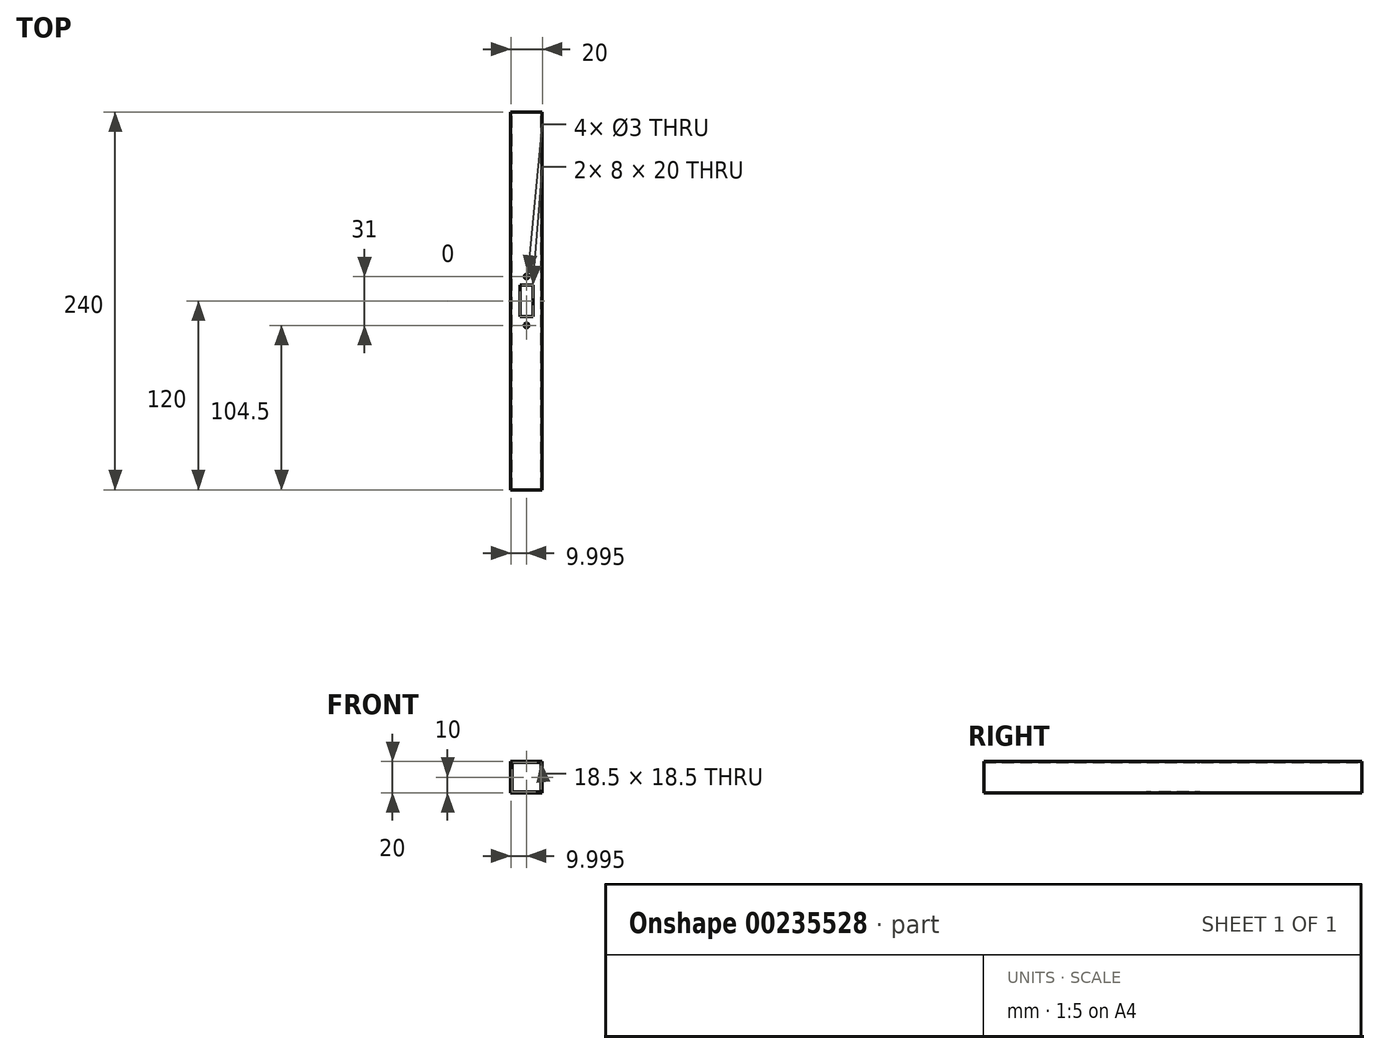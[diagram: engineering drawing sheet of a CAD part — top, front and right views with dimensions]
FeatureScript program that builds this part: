
annotation { "Feature Type Name" : "Feature", "Feature Type Description" : "" }
export const myFeature = defineFeature(function(context is Context, id is Id, definition is map)
    precondition{}
    {
        {
            var Q0;
            Q0=qCreatedBy(makeId("Front.planeOp"),FACE);
            var sketch = newSketch(context, id + "F0", { "sketchPlane" : qUnion([Q0])});
            skLineSegment(sketch, "E0.bottom", {"start": v(-34.48, 27) * mm, "end": v(-54.48, 27) * mm});
            skLineSegment(sketch, "E0.top", {"start": v(-34.48, 47) * mm, "end": v(-54.48, 47) * mm});
            skLineSegment(sketch, "E0.left", {"start": v(-34.48, 27) * mm, "end": v(-34.48, 47) * mm});
            skLineSegment(sketch, "E0.right", {"start": v(-54.48, 27) * mm, "end": v(-54.48, 47) * mm});
            skPoint(sketch, "E0.middle", {"position": v(-44.48, 37) * mm});
            skLineSegment(sketch, "E1.bottom", {"start": v(-35.23, 27.75) * mm, "end": v(-53.73, 27.75) * mm});
            skLineSegment(sketch, "E1.top", {"start": v(-35.23, 46.25) * mm, "end": v(-53.73, 46.25) * mm});
            skLineSegment(sketch, "E1.left", {"start": v(-35.23, 27.75) * mm, "end": v(-35.23, 46.25) * mm});
            skLineSegment(sketch, "E1.right", {"start": v(-53.73, 27.75) * mm, "end": v(-53.73, 46.25) * mm});
            skSolve(sketch);
        }
        {
            var Q0;
            Q0=makeQuery(id+"F0.imprint","IMPRINT",FACE,{"disambiguationData":[TD([[makeQuery(id+"F0.imprint","IMPRINT",EDGE,{"derivedFrom":sQuery(id+"F0.wireOp",EDGE,"E0.bottom")}),-1.0]])]});
            extrude(context, id + "F1", {"entities" : qUnion([Q0]), "depth" : 240 * mm});
        }
        {
            var Q0;
            Q0=makeQuery(id+"F1.opExtrude","SWEPT_FACE",FACE,{"disambiguationData":[OSD([sQuery(id+"F0.wireOp",EDGE,"E0.top")])]});
            var sketch = newSketch(context, id + "F2", { "sketchPlane" : qUnion([Q0])});
            skLineSegment(sketch, "E2.bottom", {"start": v(-54.48, 0) * mm, "end": v(-34.48, 0) * mm});
            skLineSegment(sketch, "E2.top", {"start": v(-54.48, -240) * mm, "end": v(-34.48, -240) * mm});
            skLineSegment(sketch, "E2.left", {"start": v(-54.48, 0) * mm, "end": v(-54.48, -240) * mm});
            skLineSegment(sketch, "E2.right", {"start": v(-34.48, 0) * mm, "end": v(-34.48, -240) * mm});
            skLineSegment(sketch, "E3", {"start": v(-34.48, -120) * mm, "end": v(-54.48, -120) * mm});
            skLineSegment(sketch, "E4.bottom", {"start": v(-41.48, -129) * mm, "end": v(-47.48, -129) * mm});
            skLineSegment(sketch, "E4.top", {"start": v(-41.48, -111) * mm, "end": v(-47.48, -111) * mm});
            skLineSegment(sketch, "E4.left", {"start": v(-41.48, -129) * mm, "end": v(-41.48, -111) * mm});
            skLineSegment(sketch, "E4.right", {"start": v(-47.48, -129) * mm, "end": v(-47.48, -111) * mm});
            skPoint(sketch, "E4.middle", {"position": v(-44.48, -120) * mm});
            skLineSegment(sketch, "E5.bottom", {"start": v(-40.48, -130) * mm, "end": v(-48.48, -130) * mm});
            skLineSegment(sketch, "E5.top", {"start": v(-40.48, -110) * mm, "end": v(-48.48, -110) * mm});
            skLineSegment(sketch, "E5.left", {"start": v(-40.48, -130) * mm, "end": v(-40.48, -110) * mm});
            skLineSegment(sketch, "E5.right", {"start": v(-48.48, -130) * mm, "end": v(-48.48, -110) * mm});
            skLineSegment(sketch, "E6", {"start": v(-44.48, -130) * mm, "end": v(-44.48, -135.5) * mm});
            skPoint(sketch, "E6.endSnap0", {"position": v(-44.48, -130) * mm});
            skLineSegment(sketch, "E7", {"start": v(-44.48, -110) * mm, "end": v(-44.48, -104.5) * mm});
            skPoint(sketch, "E7.endSnap0", {"position": v(-44.48, -110) * mm});
            skCircle(sketch, "E8", {"center": v(-44.48, -104.5) * mm, "radius": 1.5 * mm});
            skCircle(sketch, "E9", {"center": v(-44.48, -135.5) * mm, "radius": 1.5 * mm});
            skSolve(sketch);
        }
        {
            var Q0;
            {var subQ5=sQuery(id+"F2.wireOp",EDGE,"E4.bottom");Q0=makeQuery(id+"F2.imprint","IMPRINT",FACE,{"disambiguationData":[TD([[makeQuery(id+"F2.imprint","IMPRINT",EDGE,{"derivedFrom":subQ5}),-1.0]])]});}
            var Q1;
            {var subQ5=sQuery(id+"F2.wireOp",EDGE,"E4.top");Q1=makeQuery(id+"F2.imprint","IMPRINT",FACE,{"disambiguationData":[TD([[makeQuery(id+"F2.imprint","IMPRINT",EDGE,{"derivedFrom":subQ5}),1.0]])]});}
            var Q2;
            {var subQ6=sQuery(id+"F2.wireOp",EDGE,"E4.top");Q2=makeQuery(id+"F2.imprint","IMPRINT",FACE,{"disambiguationData":[TD([[makeQuery(id+"F2.imprint","IMPRINT",EDGE,{"derivedFrom":subQ6}),-1.0]])]});}
            var Q3;
            {var subQ0=sQuery(id+"F2.wireOp",EDGE,"E4.bottom");Q3=makeQuery(id+"F2.imprint","IMPRINT",FACE,{"disambiguationData":[TD([[makeQuery(id+"F2.imprint","IMPRINT",EDGE,{"derivedFrom":subQ0}),1.0]])]});}
            var Q4;
            Q4=makeQuery(id+"F2.imprint","IMPRINT",FACE,{"disambiguationData":[TD([[makeQuery(id+"F2.imprint","IMPRINT",EDGE,{"derivedFrom":sQuery(id+"F2.wireOp",EDGE,"E8")}),1.0]])]});
            var Q5;
            Q5=makeQuery(id+"F2.imprint","IMPRINT",FACE,{"disambiguationData":[TD([[makeQuery(id+"F2.imprint","IMPRINT",EDGE,{"derivedFrom":sQuery(id+"F2.wireOp",EDGE,"E9")}),1.0]])]});
            extrude(context, id + "F3", {"entities" : qUnion([Q0, Q1, Q2, Q3, Q4, Q5]), "operationType" : NewBodyOperationType.REMOVE, "oppositeDirection" : true, "depth" : 25 * mm});
        }
    });
